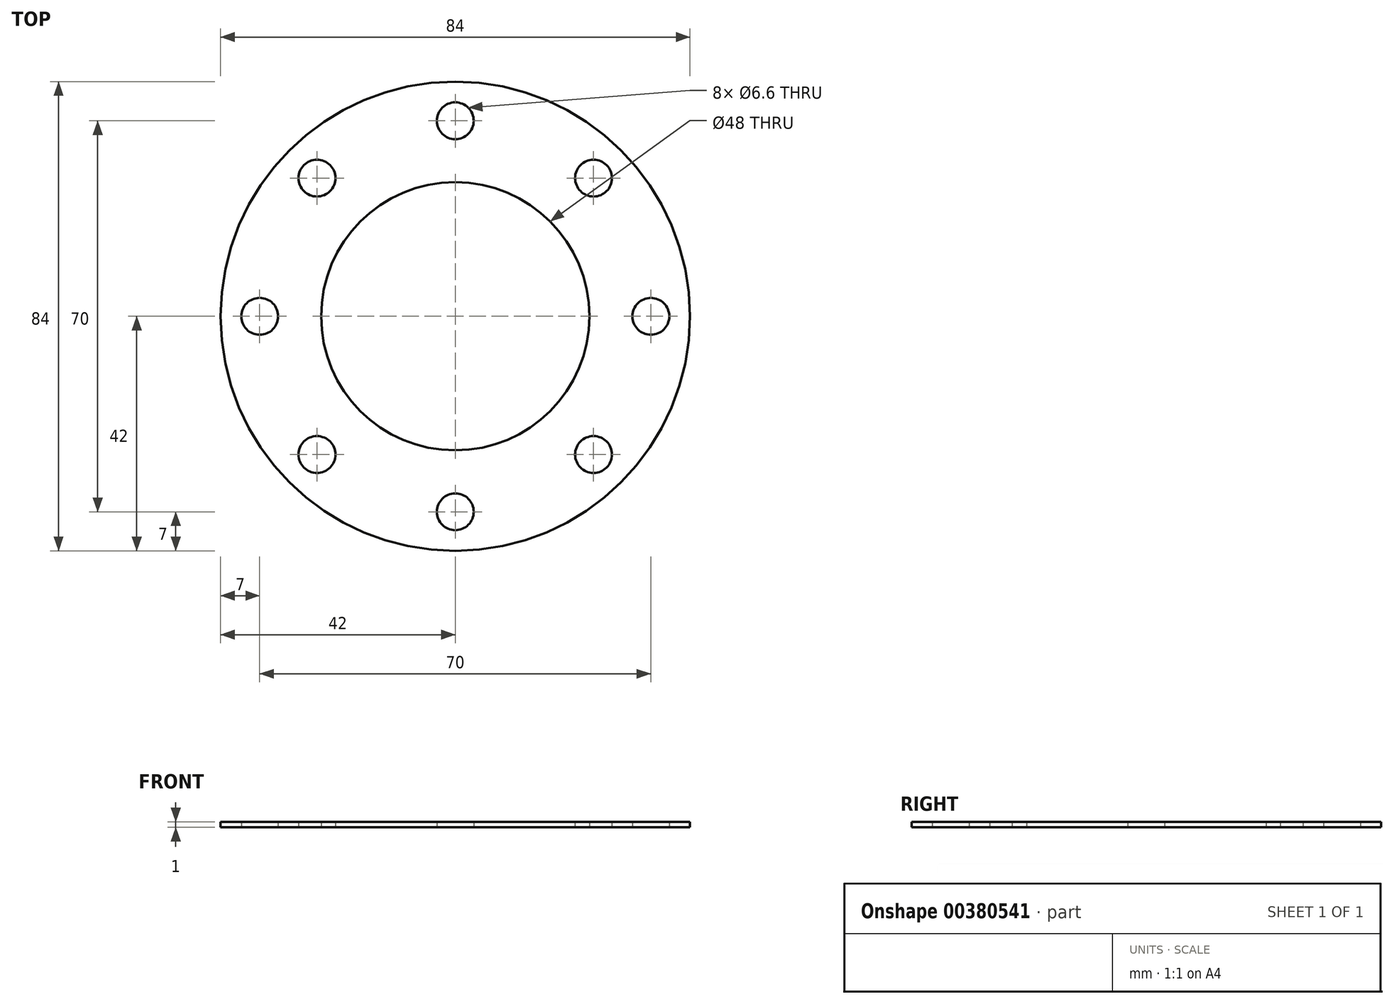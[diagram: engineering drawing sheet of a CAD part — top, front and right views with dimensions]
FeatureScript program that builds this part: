
annotation { "Feature Type Name" : "Feature", "Feature Type Description" : "" }
export const myFeature = defineFeature(function(context is Context, id is Id, definition is map)
    precondition{}
    {
        {
            var Q0;
            Q0=qCreatedBy(makeId("Top.planeOp"),FACE);
            var sketch = newSketch(context, id + "F0", { "sketchPlane" : qUnion([Q0])});
            skCircle(sketch, "E0", {"center": v(0, 0) * mm, "radius": 35 * mm, "construction": true});
            skCircle(sketch, "E1", {"center": v(0, 0) * mm, "radius": 42 * mm});
            skCircle(sketch, "E2", {"center": v(0, 0) * mm, "radius": 24 * mm});
            skLineSegment(sketch, "E3", {"start": v(0, 0) * mm, "end": v(-66.04, 66.04) * mm, "construction": true});
            skCircle(sketch, "E4", {"center": v(-24.75, 24.75) * mm, "radius": 3.3 * mm});
            skCircle(sketch, "E5", {"center": v(-35, 0) * mm, "radius": 3.3 * mm});
            skCircle(sketch, "E6", {"center": v(0, 35) * mm, "radius": 3.3 * mm});
            skCircle(sketch, "E7.MirrorC", {"center": v(-24.75, -24.75) * mm, "radius": 3.3 * mm});
            skCircle(sketch, "E8.MirrorC", {"center": v(0, -35) * mm, "radius": 3.3 * mm});
            skCircle(sketch, "E9.MirrorC", {"center": v(24.75, 24.75) * mm, "radius": 3.3 * mm});
            skCircle(sketch, "E10.MirrorC", {"center": v(35, 0) * mm, "radius": 3.3 * mm});
            skCircle(sketch, "E11.MirrorC", {"center": v(24.75, -24.75) * mm, "radius": 3.3 * mm});
            skSolve(sketch);
        }
        {
            var Q0;
            Q0=makeQuery(id+"F0.imprint","IMPRINT",FACE,{"disambiguationData":[TD([[makeQuery(id+"F0.imprint","IMPRINT",EDGE,{"derivedFrom":sQuery(id+"F0.wireOp",EDGE,"E1")}),1.0]])]});
            extrude(context, id + "F1", {"entities" : qUnion([Q0]), "depth" : 1 * mm});
        }
    });
